# Revit family: 203_RAVAV-_
name_source: partatom
category: Duct Accessories
units: mm (PartAtom-declared; Revit-internal decimal feet)

## family parameters
Always vertical = Yes
Cut with Voids When Loaded = No
Part Type = Damper
Round Connector Dimension = Use Diameter
Shared = No
Work Plane-Based = No

## types (7) — shared parameters
CAT0 = Yes
Description = VAV FLOW REGULATORS
H1 = 40 mm  [stored 0.131234 ft]
Manufacturer = Alnor
QmdConnectorList = 201;D;202;D
R1 = 40 mm  [stored 0.131234 ft]
URL = http://www.ventilation-alnor.co.uk
Y1 = 70 mm  [stored 0.229659 ft]
Z1 = 27 mm
Z2 = 53 mm
magiPartTypeId = 203
magiProductFamilyId = RAVAV-*

## per-type parameters (varying)
| type | D | H2D | L | L2D | LL | R | W2D | X1 | magiProductId |
| RAVAV-100-57-339 | 100 mm | 100 mm  [stored 0.328084 ft] | 410 mm  [stored 1.34514 ft] | 410 mm  [stored 1.34514 ft] | 205 mm  [stored 0.672572 ft] | 50 mm  [stored 0.164042 ft] | 100 mm  [stored 0.328084 ft] | 155 mm  [stored 0.50853 ft] | RAVAV-100 |
| RAVAV-400-905-5429 | 400 mm | 400 mm | 600 mm | 600 mm | 300 mm | 200 mm | 400 mm | 250 mm | RAVAV-400 |
| RAVAV-315-561-3367 | 315 mm | 315 mm | 600 mm | 600 mm | 300 mm | 158 mm | 315 mm | 250 mm | RAVAV-315 |
| RAVAV-250-353-2121 | 250 mm | 250 mm | 600 mm | 600 mm | 300 mm | 125 mm | 250 mm | 250 mm | RAVAV-250 |
| RAVAV-200-226-1357 | 200 mm | 200 mm | 410 mm  [stored 1.34514 ft] | 410 mm  [stored 1.34514 ft] | 205 mm  [stored 0.672572 ft] | 100 mm  [stored 0.328084 ft] | 200 mm | 155 mm  [stored 0.50853 ft] | RAVAV-200 |
| RAVAV-160-145-869 | 160 mm | 160 mm | 410 mm  [stored 1.34514 ft] | 410 mm  [stored 1.34514 ft] | 205 mm  [stored 0.672572 ft] | 80 mm | 160 mm | 155 mm  [stored 0.50853 ft] | RAVAV-160 |
| RAVAV-125-88-530 | 125 mm | 125 mm | 410 mm  [stored 1.34514 ft] | 410 mm  [stored 1.34514 ft] | 205 mm  [stored 0.672572 ft] | 63 mm | 125 mm | 155 mm  [stored 0.50853 ft] | RAVAV-125 |

note: column(s) folded — value = type name in every type: MC Product Code

note: [stored X ft] marks values corroborated as IEEE doubles in the binary element streams (Revit-internal decimal feet)

## geometry (parser evidence)
native form markers: Blend x4, Sweep x1
no freeform markers — native parametric forms only
